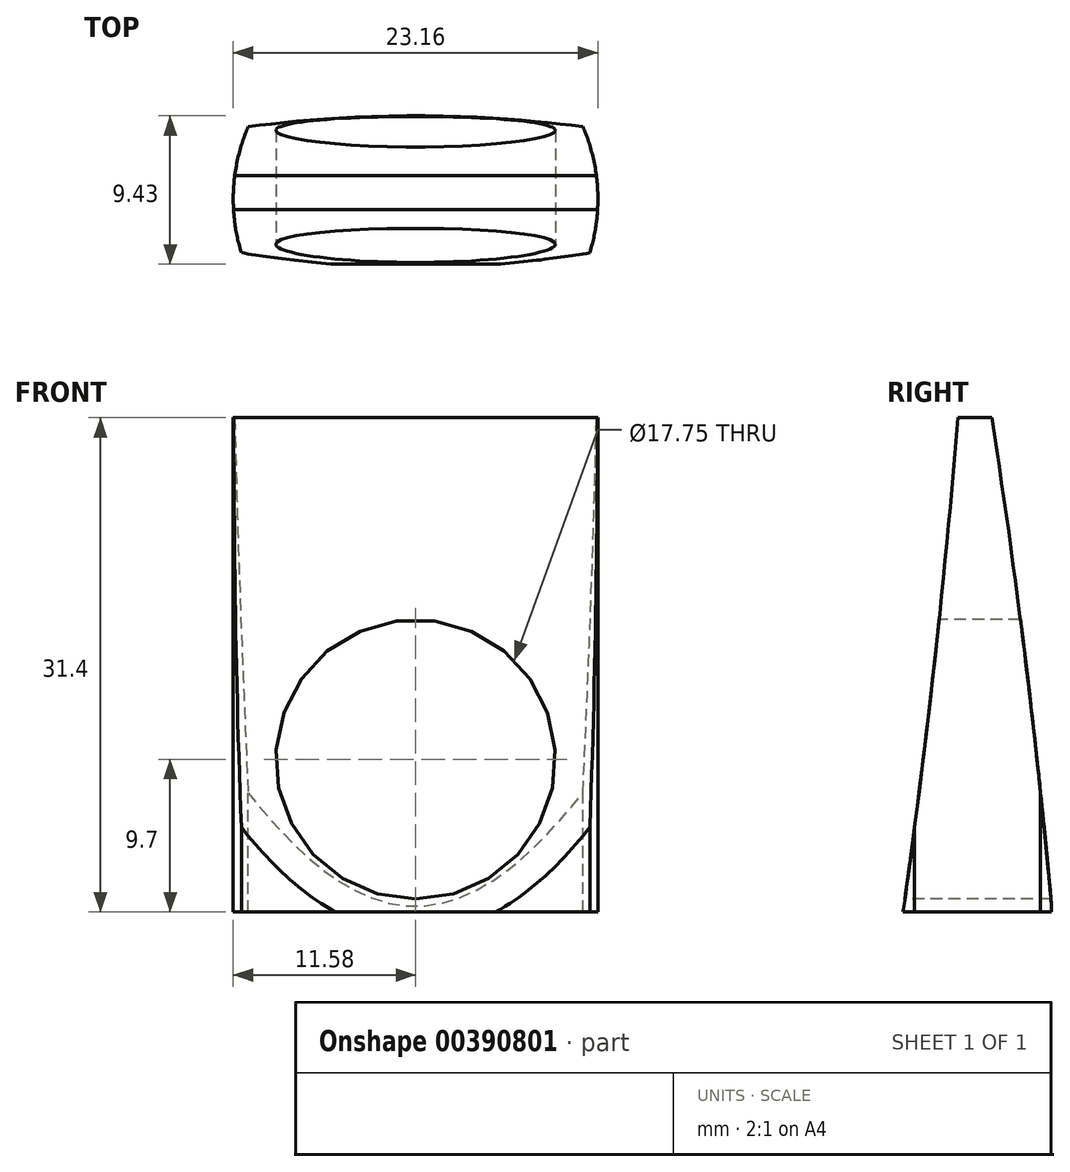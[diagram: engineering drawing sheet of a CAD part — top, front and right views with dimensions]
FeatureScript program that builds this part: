
annotation { "Feature Type Name" : "Feature", "Feature Type Description" : "" }
export const myFeature = defineFeature(function(context is Context, id is Id, definition is map)
    precondition{}
    {
        {
            var Q0;
            Q0=qCreatedBy(makeId("Front.planeOp"),FACE);
            var sketch = newSketch(context, id + "F0", { "sketchPlane" : qUnion([Q0])});
            skCircle(sketch, "E0", {"center": v(0, 0) * mm, "radius": 8.88 * mm});
            skSolve(sketch);
        }
        {
            var Q0;
            Q0=qCreatedBy(makeId("Top.planeOp"),FACE);
            var sketch = newSketch(context, id + "F1", { "sketchPlane" : qUnion([Q0])});
            skCircle(sketch, "E1", {"center": v(0, 0) * mm, "radius": 11.58 * mm});
            skLineSegment(sketch, "E2", {"start": v(-11.06, -3.41) * mm, "end": v(11.06, -3.41) * mm, "construction": true});
            skLineSegment(sketch, "E3", {"start": v(-10.63, 4.59) * mm, "end": v(10.63, 4.59) * mm, "construction": true});
            skArc(sketch, "E4", {"start": v(-11.06, -3.41) * mm, "mid": v(0, -4.34) * mm, "end": v(11.06, -3.41) * mm});
            skArc(sketch, "E5", {"start": v(10.63, 4.59) * mm, "mid": v(0, 5.29) * mm, "end": v(-10.63, 4.59) * mm});
            skSolve(sketch);
        }
        {
            var Q0;
            {var subQ0=sQuery(id+"F1.wireOp",EDGE,"E4");Q0=makeQuery(id+"F1.imprint","IMPRINT",FACE,{"disambiguationData":[TD([[makeQuery(id+"F1.imprint","IMPRINT",EDGE,{"derivedFrom":subQ0}),1.0]])]});}
            extrude(context, id + "F2", {"entities" : qUnion([Q0]), "oppositeDirection" : true, "depth" : 9.7 * mm, "hasSecondDirection" : true, "secondDirectionOppositeDirection" : false, "secondDirectionDepth" : 21.7 * mm});
        }
        {
            var Q0;
            Q0=makeQuery(id+"F0.imprint","IMPRINT",FACE,{"disambiguationData":[TD([[makeQuery(id+"F0.imprint","IMPRINT",EDGE,{"derivedFrom":sQuery(id+"F0.wireOp",EDGE,"E0")}),1.0]])]});
            extrude(context, id + "F3", {"entities" : qUnion([Q0]), "operationType" : NewBodyOperationType.REMOVE, "oppositeDirection" : true, "depth" : 25 * mm, "hasSecondDirection" : true, "secondDirectionOppositeDirection" : false, "secondDirectionDepth" : 25 * mm});
        }
        {
            var Q0;
            Q0=qCreatedBy(makeId("Right.planeOp"),FACE);
            var sketch = newSketch(context, id + "F4", { "sketchPlane" : qUnion([Q0])});
            skArc(sketch, "E6", {"start": v(6.14, -20.34) * mm, "mid": v(3.76, 5.25) * mm, "end": v(0, 30.68) * mm});
            skArc(sketch, "E7", {"start": v(-5.74, -20.34) * mm, "mid": v(-2.27, 5.1) * mm, "end": v(0, 30.68) * mm});
            skLineSegment(sketch, "E8", {"start": v(6.14, -20.34) * mm, "end": v(-5.74, -20.34) * mm});
            skArc(sketch, "E9", {"start": v(6.14, -20.34) * mm, "mid": v(0.2, 33.17) * mm, "end": v(-5.74, -20.34) * mm});
            skSolve(sketch);
        }
        {
            var Q0;
            Q0=makeQuery(id+"F4.imprint","IMPRINT",FACE,{"disambiguationData":[TD([[makeQuery(id+"F4.imprint","IMPRINT",EDGE,{"derivedFrom":sQuery(id+"F4.wireOp",EDGE,"E6")}),-1.0]])]});
            extrude(context, id + "F5", {"entities" : qUnion([Q0]), "operationType" : NewBodyOperationType.REMOVE, "oppositeDirection" : true, "depth" : 25 * mm, "hasSecondDirection" : true, "secondDirectionOppositeDirection" : false, "secondDirectionDepth" : 25 * mm});
        }
    });
